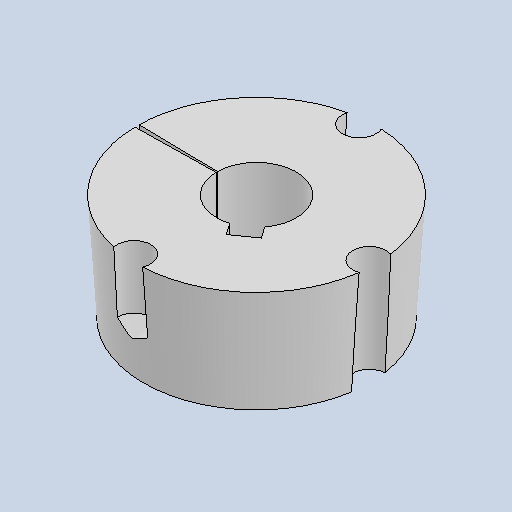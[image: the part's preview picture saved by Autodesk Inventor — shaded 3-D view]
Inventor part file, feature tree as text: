
AUTODESK INVENTOR PART (.ipt)
format: ipt  version: 2025 (Build 290162010, 162A)  size: 145,408 bytes
history: native  units: mm
features: sketch x4, hole x2, revolve x1, extrude x1
ambient origin geometry x8: Origin, YZ Plane, XZ Plane, XY Plane, X Axis, Y Axis, Z Axis, Center Point
bodies: Body1 (feature_tree)
feature tree (8):
  revolve  "Revolution1"  [1 undecoded]
  extrude  "Extrusion2"  Depth=17.485mm
  sketch  "Sketch4"  dims[d9=62.482787mm d10=9.599311mm]
  sketch  "Sketch5"  dims[d11=12.3mm d12=6.0mm d13=0.0mm d14=0.0mm d18=14.835299mm d21=14.835299mm d23=8.0mm d24=3.708mm d25=4.0mm d26=2.0mm d27=14.3117mm d28=8.0mm d29=20.594885mm d30=8.0mm d31=8.91794mm d32=4.0mm d33=2.0mm d34=90.0deg d35=15.0mm d36=20.594885mm]
  hole  "Hole1"  [1 undecoded]
  hole  "Hole2"  [1 undecoded]
  sketch  "Sketch2"  dims[d5=9.5mm d6=25.4mm]
  sketch  "Sketch3"  dims[d7=19.035mm d8=17.485mm]
note: 3 required parameter values undecoded (feature->parameter linkage not recoverable at this tier; creation-order binding heuristic only, values carry confidence <= 0.55)